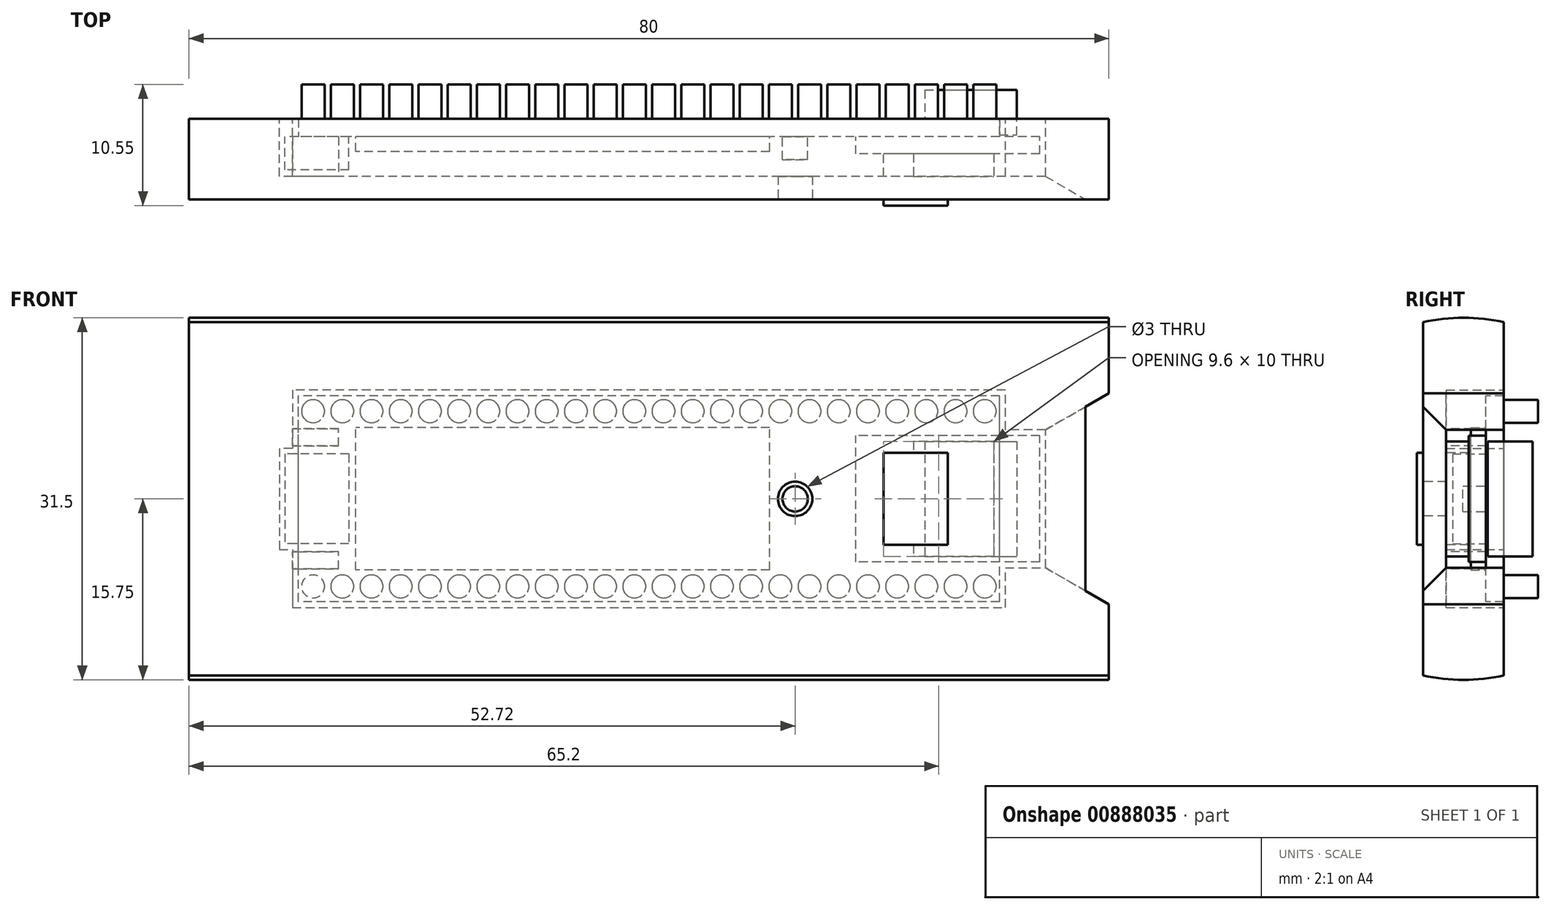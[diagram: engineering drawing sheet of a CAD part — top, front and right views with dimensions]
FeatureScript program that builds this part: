
annotation { "Feature Type Name" : "Feature", "Feature Type Description" : "" }
export const myFeature = defineFeature(function(context is Context, id is Id, definition is map)
    precondition{}
    {
        {
            var Q0;
            Q0=qCreatedBy(makeId("Front.planeOp"),FACE);
            var sketch = newSketch(context, id + "F0", { "sketchPlane" : qUnion([Q0])});
            skLineSegment(sketch, "E0.bottom", {"start": v(30.5, -8.95) * mm, "end": v(-30.5, -8.95) * mm});
            skLineSegment(sketch, "E0.top", {"start": v(30.5, 8.95) * mm, "end": v(-30.5, 8.95) * mm});
            skLineSegment(sketch, "E0.left", {"start": v(30.5, -8.95) * mm, "end": v(30.5, 8.95) * mm});
            skLineSegment(sketch, "E0.right", {"start": v(-30.5, -8.95) * mm, "end": v(-30.5, 8.95) * mm});
            skPoint(sketch, "E0.middle", {"position": v(0, 0) * mm});
            skCircle(sketch, "E1", {"center": v(12.72, 0) * mm, "radius": 1.1 * mm});
            skLineSegment(sketch, "E2.bottom", {"start": v(34, -5.5) * mm, "end": v(18, -5.5) * mm});
            skLineSegment(sketch, "E2.top", {"start": v(34, 5.5) * mm, "end": v(18, 5.5) * mm});
            skLineSegment(sketch, "E2.left", {"start": v(34, -5.5) * mm, "end": v(34, 5.5) * mm});
            skLineSegment(sketch, "E2.right", {"start": v(18, -5.5) * mm, "end": v(18, 5.5) * mm});
            skPoint(sketch, "E2.middle", {"position": v(26, 0) * mm});
            skLineSegment(sketch, "E3.bottom", {"start": v(-26.1, 3.9) * mm, "end": v(-31.65, 3.9) * mm});
            skLineSegment(sketch, "E3.top", {"start": v(-26.1, -3.9) * mm, "end": v(-31.65, -3.9) * mm});
            skLineSegment(sketch, "E3.left", {"start": v(-26.1, 3.9) * mm, "end": v(-26.1, -3.9) * mm});
            skLineSegment(sketch, "E3.right", {"start": v(-31.65, 3.9) * mm, "end": v(-31.65, -3.9) * mm});
            skPoint(sketch, "E3.middle", {"position": v(-28.87, 0) * mm});
            skLineSegment(sketch, "E4.bottom", {"start": v(10.5, -6.2) * mm, "end": v(-25.5, -6.2) * mm});
            skLineSegment(sketch, "E4.top", {"start": v(10.5, 6.2) * mm, "end": v(-25.5, 6.2) * mm});
            skLineSegment(sketch, "E4.left", {"start": v(10.5, -6.2) * mm, "end": v(10.5, 6.2) * mm});
            skLineSegment(sketch, "E4.right", {"start": v(-25.5, -6.2) * mm, "end": v(-25.5, 6.2) * mm});
            skPoint(sketch, "E4.middle", {"position": v(-7.5, 0) * mm});
            skSolve(sketch);
        }
        {
            var Q0;
            {var subQ8=sQuery(id+"F0.wireOp",EDGE,"E0.bottom");Q0=makeQuery(id+"F0.imprint","IMPRINT",FACE,{"disambiguationData":[TD([[makeQuery(id+"F0.imprint","IMPRINT",EDGE,{"derivedFrom":subQ8}),-1.0]])]});}
            var Q1;
            {var subQ5=sQuery(id+"F0.wireOp",EDGE,"E3.left");Q1=makeQuery(id+"F0.imprint","IMPRINT",FACE,{"disambiguationData":[TD([[makeQuery(id+"F0.imprint","IMPRINT",EDGE,{"derivedFrom":subQ5}),-1.0]])]});}
            var Q2;
            {var subQ5=sQuery(id+"F0.wireOp",EDGE,"E2.right");Q2=makeQuery(id+"F0.imprint","IMPRINT",FACE,{"disambiguationData":[TD([[makeQuery(id+"F0.imprint","IMPRINT",EDGE,{"derivedFrom":subQ5}),-1.0]])]});}
            var Q3;
            Q3=makeQuery(id+"F0.imprint","IMPRINT",FACE,{"disambiguationData":[TD([[makeQuery(id+"F0.imprint","IMPRINT",EDGE,{"derivedFrom":sQuery(id+"F0.wireOp",EDGE,"E1")}),1.0]])]});
            var Q4;
            Q4=makeQuery(id+"F0.imprint","IMPRINT",FACE,{"disambiguationData":[TD([[makeQuery(id+"F0.imprint","IMPRINT",EDGE,{"derivedFrom":sQuery(id+"F0.wireOp",EDGE,"E4.bottom")}),-1.0]])]});
            extrude(context, id + "F1", {"entities" : qUnion([Q0, Q1, Q2, Q3, Q4]), "oppositeDirection" : true, "depth" : 1.55 * mm, "offsetDistance" : 25 * mm});
        }
        {
            var Q0;
            Q0=makeQuery(id+"F0.imprint","IMPRINT",FACE,{"disambiguationData":[TD([[makeQuery(id+"F0.imprint","IMPRINT",EDGE,{"derivedFrom":sQuery(id+"F0.wireOp",EDGE,"E1")}),1.0]])]});
            extrude(context, id + "F2", {"entities" : qUnion([Q0]), "operationType" : NewBodyOperationType.ADD, "depth" : 2 * mm, "offsetDistance" : 25 * mm});
        }
        {
            var Q0;
            {var subQ5=sQuery(id+"F0.wireOp",EDGE,"E3.left");Q0=makeQuery(id+"F0.imprint","IMPRINT",FACE,{"disambiguationData":[TD([[makeQuery(id+"F0.imprint","IMPRINT",EDGE,{"derivedFrom":subQ5}),-1.0]])]});}
            var Q1;
            {var subQ5=sQuery(id+"F0.wireOp",EDGE,"E3.right");Q1=makeQuery(id+"F0.imprint","IMPRINT",FACE,{"disambiguationData":[TD([[makeQuery(id+"F0.imprint","IMPRINT",EDGE,{"derivedFrom":subQ5}),1.0]])]});}
            extrude(context, id + "F3", {"entities" : qUnion([Q0, Q1]), "operationType" : NewBodyOperationType.ADD, "depth" : 2.9 * mm, "offsetDistance" : 25 * mm});
        }
        {
            var Q0;
            {var subQ5=sQuery(id+"F0.wireOp",EDGE,"E2.left");Q0=makeQuery(id+"F0.imprint","IMPRINT",FACE,{"disambiguationData":[TD([[makeQuery(id+"F0.imprint","IMPRINT",EDGE,{"derivedFrom":subQ5}),1.0]])]});}
            var Q1;
            {var subQ5=sQuery(id+"F0.wireOp",EDGE,"E2.right");Q1=makeQuery(id+"F0.imprint","IMPRINT",FACE,{"disambiguationData":[TD([[makeQuery(id+"F0.imprint","IMPRINT",EDGE,{"derivedFrom":subQ5}),-1.0]])]});}
            extrude(context, id + "F4", {"entities" : qUnion([Q0, Q1]), "operationType" : NewBodyOperationType.ADD, "depth" : 1.5 * mm, "offsetDistance" : 25 * mm});
        }
        {
            var Q0;
            Q0=makeQuery(id+"F0.imprint","IMPRINT",FACE,{"disambiguationData":[TD([[makeQuery(id+"F0.imprint","IMPRINT",EDGE,{"derivedFrom":sQuery(id+"F0.wireOp",EDGE,"E4.bottom")}),-1.0]])]});
            extrude(context, id + "F5", {"entities" : qUnion([Q0]), "operationType" : NewBodyOperationType.ADD, "depth" : 1.3 * mm, "offsetDistance" : 25 * mm});
        }
        {
            var Q0;
            Q0=makeQuery(id+"F1.opExtrude","CAP_FACE",FACE,{"disambiguationData":[OSD([sQuery(id+"F0.wireOp",EDGE,"E0.bottom"),sQuery(id+"F0.wireOp",EDGE,"E0.top"),sQuery(id+"F0.wireOp",EDGE,"E0.left"),sQuery(id+"F0.wireOp",EDGE,"E0.right")])],"isStart":false});
            var sketch = newSketch(context, id + "F6", { "sketchPlane" : qUnion([Q0])});
            skCircle(sketch, "E5", {"center": v(29.21, -7.62) * mm, "radius": 1 * mm});
            skCircle(sketch, "E6.0.1.0", {"center": v(29.21, 7.62) * mm, "radius": 1 * mm});
            skCircle(sketch, "E6.1.0.0", {"center": v(26.67, -7.62) * mm, "radius": 1 * mm});
            skCircle(sketch, "E6.1.1.0", {"center": v(26.67, 7.62) * mm, "radius": 1 * mm});
            skCircle(sketch, "E6.2.0.0", {"center": v(24.13, -7.62) * mm, "radius": 1 * mm});
            skCircle(sketch, "E6.2.1.0", {"center": v(24.13, 7.62) * mm, "radius": 1 * mm});
            skCircle(sketch, "E6.3.0.0", {"center": v(21.6, -7.62) * mm, "radius": 1 * mm});
            skCircle(sketch, "E6.3.1.0", {"center": v(21.6, 7.62) * mm, "radius": 1 * mm});
            skCircle(sketch, "E6.4.0.0", {"center": v(19.05, -7.62) * mm, "radius": 1 * mm});
            skCircle(sketch, "E6.4.1.0", {"center": v(19.05, 7.62) * mm, "radius": 1 * mm});
            skCircle(sketch, "E6.5.0.0", {"center": v(16.51, -7.62) * mm, "radius": 1 * mm});
            skCircle(sketch, "E6.5.1.0", {"center": v(16.51, 7.62) * mm, "radius": 1 * mm});
            skCircle(sketch, "E6.6.0.0", {"center": v(13.97, -7.62) * mm, "radius": 1 * mm});
            skCircle(sketch, "E6.6.1.0", {"center": v(13.97, 7.62) * mm, "radius": 1 * mm});
            skCircle(sketch, "E6.7.0.0", {"center": v(11.43, -7.62) * mm, "radius": 1 * mm});
            skCircle(sketch, "E6.7.1.0", {"center": v(11.43, 7.62) * mm, "radius": 1 * mm});
            skCircle(sketch, "E6.8.0.0", {"center": v(8.9, -7.62) * mm, "radius": 1 * mm});
            skCircle(sketch, "E6.8.1.0", {"center": v(8.9, 7.62) * mm, "radius": 1 * mm});
            skCircle(sketch, "E6.9.0.0", {"center": v(6.35, -7.62) * mm, "radius": 1 * mm});
            skCircle(sketch, "E6.9.1.0", {"center": v(6.35, 7.62) * mm, "radius": 1 * mm});
            skCircle(sketch, "E6.10.0.0", {"center": v(3.81, -7.62) * mm, "radius": 1 * mm});
            skCircle(sketch, "E6.10.1.0", {"center": v(3.81, 7.62) * mm, "radius": 1 * mm});
            skCircle(sketch, "E6.11.0.0", {"center": v(1.27, -7.62) * mm, "radius": 1 * mm});
            skCircle(sketch, "E6.11.1.0", {"center": v(1.27, 7.62) * mm, "radius": 1 * mm});
            skCircle(sketch, "E6.12.0.0", {"center": v(-1.27, -7.62) * mm, "radius": 1 * mm});
            skCircle(sketch, "E6.12.1.0", {"center": v(-1.27, 7.62) * mm, "radius": 1 * mm});
            skCircle(sketch, "E6.13.0.0", {"center": v(-3.81, -7.62) * mm, "radius": 1 * mm});
            skCircle(sketch, "E6.13.1.0", {"center": v(-3.81, 7.62) * mm, "radius": 1 * mm});
            skCircle(sketch, "E6.14.0.0", {"center": v(-6.35, -7.62) * mm, "radius": 1 * mm});
            skCircle(sketch, "E6.14.1.0", {"center": v(-6.35, 7.62) * mm, "radius": 1 * mm});
            skCircle(sketch, "E6.15.0.0", {"center": v(-8.9, -7.62) * mm, "radius": 1 * mm});
            skCircle(sketch, "E6.15.1.0", {"center": v(-8.9, 7.62) * mm, "radius": 1 * mm});
            skCircle(sketch, "E6.16.0.0", {"center": v(-11.43, -7.62) * mm, "radius": 1 * mm});
            skCircle(sketch, "E6.16.1.0", {"center": v(-11.43, 7.62) * mm, "radius": 1 * mm});
            skCircle(sketch, "E6.17.0.0", {"center": v(-13.97, -7.62) * mm, "radius": 1 * mm});
            skCircle(sketch, "E6.17.1.0", {"center": v(-13.97, 7.62) * mm, "radius": 1 * mm});
            skCircle(sketch, "E6.18.0.0", {"center": v(-16.51, -7.62) * mm, "radius": 1 * mm});
            skCircle(sketch, "E6.18.1.0", {"center": v(-16.51, 7.62) * mm, "radius": 1 * mm});
            skCircle(sketch, "E6.19.0.0", {"center": v(-19.05, -7.62) * mm, "radius": 1 * mm});
            skCircle(sketch, "E6.19.1.0", {"center": v(-19.05, 7.62) * mm, "radius": 1 * mm});
            skCircle(sketch, "E6.20.0.0", {"center": v(-21.6, -7.62) * mm, "radius": 1 * mm});
            skCircle(sketch, "E6.20.1.0", {"center": v(-21.6, 7.62) * mm, "radius": 1 * mm});
            skCircle(sketch, "E6.21.0.0", {"center": v(-24.13, -7.62) * mm, "radius": 1 * mm});
            skCircle(sketch, "E6.21.1.0", {"center": v(-24.13, 7.62) * mm, "radius": 1 * mm});
            skCircle(sketch, "E6.22.0.0", {"center": v(-26.67, -7.62) * mm, "radius": 1 * mm});
            skCircle(sketch, "E6.22.1.0", {"center": v(-26.67, 7.62) * mm, "radius": 1 * mm});
            skCircle(sketch, "E6.23.0.0", {"center": v(-29.21, -7.62) * mm, "radius": 1 * mm});
            skCircle(sketch, "E6.23.1.0", {"center": v(-29.21, 7.62) * mm, "radius": 1 * mm});
            skLineSegment(sketch, "E6.direction1", {"start": v(29.21, -7.62) * mm, "end": v(26.67, -7.62) * mm, "construction": true});
            skLineSegment(sketch, "E6.direction2", {"start": v(29.21, -7.62) * mm, "end": v(29.21, 7.62) * mm, "construction": true});
            skSolve(sketch);
        }
        {
            var Q0;
            Q0=qSketchRegion(id+"F6",true);
            extrude(context, id + "F7", {"entities" : qUnion([Q0]), "operationType" : NewBodyOperationType.ADD, "depth" : 3 * mm, "offsetDistance" : 25 * mm});
        }
        {
            var Q0;
            Q0=makeQuery(id+"F4.opExtrude","CAP_FACE",FACE,{"disambiguationData":[OSD([sQuery(id+"F0.wireOp",EDGE,"E2.bottom"),sQuery(id+"F0.wireOp",EDGE,"E2.top"),sQuery(id+"F0.wireOp",EDGE,"E2.left"),sQuery(id+"F0.wireOp",EDGE,"E2.right")])],"isStart":false});
            var sketch = newSketch(context, id + "F8", { "sketchPlane" : qUnion([Q0])});
            skLineSegment(sketch, "E7.bottom", {"start": v(26, -4) * mm, "end": v(20.4, -4) * mm});
            skLineSegment(sketch, "E7.top", {"start": v(26, 4) * mm, "end": v(20.4, 4) * mm});
            skLineSegment(sketch, "E7.left", {"start": v(26, -4) * mm, "end": v(26, 4) * mm});
            skLineSegment(sketch, "E7.right", {"start": v(20.4, -4) * mm, "end": v(20.4, 4) * mm});
            skPoint(sketch, "E7.middle", {"position": v(23.2, 0) * mm});
            skSolve(sketch);
        }
        {
            var Q0;
            Q0=makeQuery(id+"F1.opExtrude","CAP_FACE",FACE,{"disambiguationData":[OSD([sQuery(id+"F0.wireOp",EDGE,"E0.bottom"),sQuery(id+"F0.wireOp",EDGE,"E0.top"),sQuery(id+"F0.wireOp",EDGE,"E0.left"),sQuery(id+"F0.wireOp",EDGE,"E0.right")])],"isStart":false});
            var sketch = newSketch(context, id + "F9", { "sketchPlane" : qUnion([Q0])});
            skLineSegment(sketch, "E8.bottom", {"start": v(-24, 5) * mm, "end": v(-32, 5) * mm});
            skLineSegment(sketch, "E8.top", {"start": v(-24, -5) * mm, "end": v(-32, -5) * mm});
            skLineSegment(sketch, "E8.left", {"start": v(-24, 5) * mm, "end": v(-24, -5) * mm});
            skLineSegment(sketch, "E8.right", {"start": v(-32, 5) * mm, "end": v(-32, -5) * mm});
            skPoint(sketch, "E8.middle", {"position": v(-28, 0) * mm});
            skLineSegment(sketch, "E9", {"start": v(-30.5, -5) * mm, "end": v(-30.5, 5) * mm});
            skSolve(sketch);
        }
        {
            var Q0;
            Q0=makeQuery(id+"F8.imprint","IMPRINT",FACE,{"disambiguationData":[TD([[makeQuery(id+"F8.imprint","IMPRINT",EDGE,{"derivedFrom":sQuery(id+"F8.wireOp",EDGE,"E7.bottom")}),-1.0]])]});
            extrude(context, id + "F10", {"entities" : qUnion([Q0]), "depth" : 4.5 * mm, "offsetDistance" : 25 * mm});
        }
        {
            var Q0;
            {var subQ0=sQuery(id+"F9.wireOp",EDGE,"E8.right");Q0=makeQuery(id+"F9.imprint","IMPRINT",FACE,{"disambiguationData":[TD([[makeQuery(id+"F9.imprint","IMPRINT",EDGE,{"derivedFrom":subQ0}),1.0]])]});}
            extrude(context, id + "F11", {"entities" : qUnion([Q0]), "oppositeDirection" : true, "depth" : 1.4 * mm, "offsetDistance" : 25 * mm});
        }
        {
            var Q0;
            {var subQ0=sQuery(id+"F9.wireOp",EDGE,"E8.right");Q0=makeQuery(id+"F9.imprint","IMPRINT",FACE,{"disambiguationData":[TD([[makeQuery(id+"F9.imprint","IMPRINT",EDGE,{"derivedFrom":subQ0}),1.0]])]});}
            var Q1;
            {var subQ0=sQuery(id+"F9.wireOp",EDGE,"E8.left");Q1=makeQuery(id+"F9.imprint","IMPRINT",FACE,{"disambiguationData":[TD([[makeQuery(id+"F9.imprint","IMPRINT",EDGE,{"derivedFrom":subQ0}),-1.0]])]});}
            extrude(context, id + "F12", {"entities" : qUnion([Q0, Q1]), "operationType" : NewBodyOperationType.ADD, "depth" : 2.5 * mm, "offsetDistance" : 25 * mm});
        }
        {
            var Q0;
            {var subQ1=sQuery(id+"F9.wireOp",EDGE,"E8.left");Q0=makeQuery(id+"F9.imprint","IMPRINT",FACE,{"disambiguationData":[TD([[makeQuery(id+"F9.imprint","IMPRINT",EDGE,{"derivedFrom":subQ1}),1.0]])]});}
            var sketch = newSketch(context, id + "F13", { "sketchPlane" : qUnion([Q0])});
            skLineSegment(sketch, "E10.bottom", {"start": v(-40, -17.5) * mm, "end": v(40, -17.5) * mm});
            skLineSegment(sketch, "E10.top", {"start": v(-40, 17.5) * mm, "end": v(40, 17.5) * mm});
            skLineSegment(sketch, "E10.left", {"start": v(-40, -17.5) * mm, "end": v(-40, 17.5) * mm});
            skLineSegment(sketch, "E10.right", {"start": v(40, -17.5) * mm, "end": v(40, 17.5) * mm});
            skPoint(sketch, "E10.middle", {"position": v(0, 0) * mm});
            skLineSegment(sketch, "E11", {"start": v(30.5, 8.95) * mm, "end": v(30.5, 3.9) * mm, "construction": true});
            skLineSegment(sketch, "E12", {"start": v(30.5, 3.9) * mm, "end": v(31.65, 3.9) * mm, "construction": true});
            skLineSegment(sketch, "E13", {"start": v(31.65, 3.9) * mm, "end": v(31.65, -3.9) * mm, "construction": true});
            skLineSegment(sketch, "E14", {"start": v(31.65, -3.9) * mm, "end": v(30.5, -3.9) * mm, "construction": true});
            skLineSegment(sketch, "E15", {"start": v(30.5, -3.9) * mm, "end": v(30.5, -8.95) * mm, "construction": true});
            skLineSegment(sketch, "E16", {"start": v(30.5, -8.95) * mm, "end": v(-30.5, -8.95) * mm, "construction": true});
            skLineSegment(sketch, "E17", {"start": v(-30.5, -8.95) * mm, "end": v(-30.5, -5.5) * mm, "construction": true});
            skLineSegment(sketch, "E18", {"start": v(-30.5, -5.5) * mm, "end": v(-34, -5.5) * mm, "construction": true});
            skLineSegment(sketch, "E19", {"start": v(-34, -5.5) * mm, "end": v(-34, 5.5) * mm, "construction": true});
            skLineSegment(sketch, "E20", {"start": v(-34, 5.5) * mm, "end": v(-30.5, 5.5) * mm, "construction": true});
            skLineSegment(sketch, "E21", {"start": v(-30.5, 5.5) * mm, "end": v(-30.5, 8.95) * mm, "construction": true});
            skLineSegment(sketch, "E22", {"start": v(-30.5, 8.95) * mm, "end": v(30.5, 8.95) * mm, "construction": true});
            skLineSegment(sketch, "E23.0", {"start": v(-31, 6) * mm, "end": v(-31, 9.45) * mm});
            skLineSegment(sketch, "E23.1", {"start": v(32.15, -4.4) * mm, "end": v(31, -4.4) * mm});
            skLineSegment(sketch, "E23.2", {"start": v(32.15, 4.4) * mm, "end": v(32.15, -4.4) * mm});
            skLineSegment(sketch, "E23.3", {"start": v(31, 4.4) * mm, "end": v(32.15, 4.4) * mm});
            skLineSegment(sketch, "E23.4", {"start": v(31, 9.45) * mm, "end": v(31, 4.4) * mm});
            skLineSegment(sketch, "E23.5", {"start": v(31, -4.4) * mm, "end": v(31, -9.45) * mm});
            skLineSegment(sketch, "E23.6", {"start": v(-31, 9.45) * mm, "end": v(31, 9.45) * mm});
            skLineSegment(sketch, "E23.7", {"start": v(31, -9.45) * mm, "end": v(-31, -9.45) * mm});
            skLineSegment(sketch, "E23.8", {"start": v(-31, -9.45) * mm, "end": v(-31, -6) * mm});
            skLineSegment(sketch, "E23.9", {"start": v(-31, -6) * mm, "end": v(-34.5, -6) * mm});
            skLineSegment(sketch, "E23.10", {"start": v(-34.5, -6) * mm, "end": v(-34.5, 6) * mm});
            skLineSegment(sketch, "E23.11", {"start": v(-34.5, 6) * mm, "end": v(-31, 6) * mm});
            skLineSegment(sketch, "E24", {"start": v(31, 4.4) * mm, "end": v(31, -4.4) * mm});
            skLineSegment(sketch, "E25", {"start": v(-31, 6) * mm, "end": v(-31, -6) * mm});
            skLineSegment(sketch, "E26.bottom", {"start": v(27, 2.25) * mm, "end": v(29.5, 2.25) * mm});
            skLineSegment(sketch, "E26.top", {"start": v(27, -2.25) * mm, "end": v(29.5, -2.25) * mm});
            skLineSegment(sketch, "E26.left", {"start": v(27, 2.25) * mm, "end": v(27, -2.25) * mm});
            skLineSegment(sketch, "E26.right", {"start": v(29.5, 2.25) * mm, "end": v(29.5, -2.25) * mm});
            skPoint(sketch, "E26.middle", {"position": v(28.25, 0) * mm});
            skLineSegment(sketch, "E27.bottom", {"start": v(-25.25, -3.75) * mm, "end": v(-20.75, -3.75) * mm});
            skLineSegment(sketch, "E27.top", {"start": v(-25.25, 3.75) * mm, "end": v(-20.75, 3.75) * mm});
            skLineSegment(sketch, "E27.left", {"start": v(-25.25, -3.75) * mm, "end": v(-25.25, 3.75) * mm});
            skLineSegment(sketch, "E27.right", {"start": v(-20.75, -3.75) * mm, "end": v(-20.75, 3.75) * mm});
            skPoint(sketch, "E27.middle", {"position": v(-23, 0) * mm});
            skSolve(sketch);
        }
        {
            var Q0;
            Q0=makeQuery(id+"F13.imprint","IMPRINT",FACE,{"disambiguationData":[TD([[makeQuery(id+"F13.imprint","IMPRINT",EDGE,{"derivedFrom":sQuery(id+"F13.wireOp",EDGE,"E10.bottom")}),1.0]])]});
            extrude(context, id + "F14", {"entities" : qUnion([Q0]), "oppositeDirection" : true, "depth" : 7 * mm, "offsetDistance" : 25 * mm});
        }
        {
            var Q0;
            Q0=makeQuery(id+"F14.opExtrude","CAP_FACE",FACE,{"disambiguationData":[OSD([sQuery(id+"F13.wireOp",EDGE,"E10.bottom"),sQuery(id+"F13.wireOp",EDGE,"E10.top"),sQuery(id+"F13.wireOp",EDGE,"E10.left"),sQuery(id+"F13.wireOp",EDGE,"E10.right"),sQuery(id+"F13.wireOp",EDGE,"E23.0"),sQuery(id+"F13.wireOp",EDGE,"E23.1"),sQuery(id+"F13.wireOp",EDGE,"E23.2"),sQuery(id+"F13.wireOp",EDGE,"E23.3"),sQuery(id+"F13.wireOp",EDGE,"E23.4"),sQuery(id+"F13.wireOp",EDGE,"E23.5"),sQuery(id+"F13.wireOp",EDGE,"E23.6"),sQuery(id+"F13.wireOp",EDGE,"E23.7"),sQuery(id+"F13.wireOp",EDGE,"E23.8"),sQuery(id+"F13.wireOp",EDGE,"E23.9"),sQuery(id+"F13.wireOp",EDGE,"E23.10"),sQuery(id+"F13.wireOp",EDGE,"E23.11")])],"isStart":false});
            var sketch = newSketch(context, id + "F15", { "sketchPlane" : qUnion([Q0])});
            skLineSegment(sketch, "E28.bottom", {"start": v(-31, 6.1) * mm, "end": v(-27, 6.1) * mm});
            skLineSegment(sketch, "E28.top", {"start": v(-31, 4.6) * mm, "end": v(-27, 4.6) * mm});
            skLineSegment(sketch, "E28.left", {"start": v(-31, 6.1) * mm, "end": v(-31, 4.6) * mm});
            skLineSegment(sketch, "E28.right", {"start": v(-27, 6.1) * mm, "end": v(-27, 4.6) * mm});
            skLineSegment(sketch, "E29.bottom", {"start": v(-27, -4.6) * mm, "end": v(-31, -4.6) * mm});
            skLineSegment(sketch, "E29.top", {"start": v(-27, -6.1) * mm, "end": v(-31, -6.1) * mm});
            skLineSegment(sketch, "E29.left", {"start": v(-27, -4.6) * mm, "end": v(-27, -6.1) * mm});
            skLineSegment(sketch, "E29.right", {"start": v(-31, -4.6) * mm, "end": v(-31, -6.1) * mm});
            skLineSegment(sketch, "E30.bottom", {"start": v(23, -5) * mm, "end": v(30, -5) * mm});
            skLineSegment(sketch, "E30.top", {"start": v(23, 5) * mm, "end": v(30, 5) * mm});
            skLineSegment(sketch, "E30.left", {"start": v(23, -5) * mm, "end": v(23, 5) * mm});
            skLineSegment(sketch, "E30.right", {"start": v(30, -5) * mm, "end": v(30, 5) * mm});
            skPoint(sketch, "E30.middle", {"position": v(26.5, 0) * mm});
            skSolve(sketch);
        }
        {
            var Q0;
            Q0=makeQuery(id+"F15.imprint","IMPRINT",FACE,{"disambiguationData":[TD([[makeQuery(id+"F15.imprint","IMPRINT",EDGE,{"derivedFrom":makeQuery(id+"F14.opExtrude","CAP_EDGE",EDGE,{"disambiguationData":[OSD([sQuery(id+"F13.wireOp",EDGE,"E23.0")])],"isStart":false})}),1.0]])]});
            extrude(context, id + "F16", {"entities" : qUnion([Q0]), "operationType" : NewBodyOperationType.ADD, "oppositeDirection" : true, "depth" : 2 * mm, "offsetDistance" : 25 * mm});
        }
        {
            var Q0;
            Q0=makeQuery(id+"F15.imprint","IMPRINT",FACE,{"disambiguationData":[TD([[makeQuery(id+"F15.imprint","IMPRINT",EDGE,{"derivedFrom":sQuery(id+"F15.wireOp",EDGE,"E28.bottom")}),-1.0]])]});
            var Q1;
            Q1=makeQuery(id+"F15.imprint","IMPRINT",FACE,{"disambiguationData":[TD([[makeQuery(id+"F15.imprint","IMPRINT",EDGE,{"derivedFrom":sQuery(id+"F15.wireOp",EDGE,"E29.bottom")}),1.0]])]});
            var Q2;
            Q2=makeQuery(id+"F1.opExtrude","CAP_FACE",FACE,{"disambiguationData":[OSD([sQuery(id+"F0.wireOp",EDGE,"E0.bottom"),sQuery(id+"F0.wireOp",EDGE,"E0.top"),sQuery(id+"F0.wireOp",EDGE,"E0.left"),sQuery(id+"F0.wireOp",EDGE,"E0.right")])],"isStart":true});
            extrude(context, id + "F17", {"entities" : qUnion([Q0, Q1]), "operationType" : NewBodyOperationType.ADD, "endBound" : BoundingType.UP_TO_SURFACE, "oppositeDirection" : true, "depth" : 5 * mm, "endBoundEntityFace" : qUnion([Q2]), "offsetDistance" : 25 * mm});
        }
        {
            var Q0;
            Q0=makeQuery(id+"F15.imprint","IMPRINT",FACE,{"disambiguationData":[TD([[makeQuery(id+"F15.imprint","IMPRINT",EDGE,{"derivedFrom":sQuery(id+"F15.wireOp",EDGE,"E30.bottom")}),1.0]])]});
            var Q1;
            Q1=makeQuery(id+"F4.opExtrude","CAP_FACE",FACE,{"disambiguationData":[OSD([sQuery(id+"F0.wireOp",EDGE,"E2.bottom"),sQuery(id+"F0.wireOp",EDGE,"E2.top"),sQuery(id+"F0.wireOp",EDGE,"E2.left"),sQuery(id+"F0.wireOp",EDGE,"E2.right")])],"isStart":false});
            extrude(context, id + "F18", {"entities" : qUnion([Q0]), "operationType" : NewBodyOperationType.ADD, "endBound" : BoundingType.UP_TO_SURFACE, "oppositeDirection" : true, "depth" : 25 * mm, "endBoundEntityFace" : qUnion([Q1]), "offsetDistance" : 25 * mm});
        }
        {
            var Q0;
            {var subQ3=sQuery(id+"F15.wireOp",EDGE,"E28.left");Q0=makeQuery(id+"F15.imprint","IMPRINT",FACE,{"disambiguationData":[TD([[makeQuery(id+"F15.imprint","IMPRINT",EDGE,{"derivedFrom":subQ3}),-1.0]])]});}
            var sketch = newSketch(context, id + "F19", { "sketchPlane" : qUnion([Q0])});
            skCircle(sketch, "E31", {"center": v(12.72, 0) * mm, "radius": 1.5 * mm});
            skSolve(sketch);
        }
        {
            var Q0;
            Q0=makeQuery(id+"F19.imprint","IMPRINT",FACE,{"disambiguationData":[TD([[makeQuery(id+"F19.imprint","IMPRINT",EDGE,{"derivedFrom":sQuery(id+"F19.wireOp",EDGE,"E31")}),1.0]])]});
            extrude(context, id + "F20", {"entities" : qUnion([Q0]), "operationType" : NewBodyOperationType.REMOVE, "endBound" : BoundingType.UP_TO_NEXT, "oppositeDirection" : true, "depth" : 25 * mm, "offsetDistance" : 25 * mm});
        }
        {
            var Q0;
            Q0=makeQuery(id+"F14.opExtrude","SWEPT_FACE",FACE,{"disambiguationData":[OSD([sQuery(id+"F13.wireOp",EDGE,"E23.10")])]});
            var sketch = newSketch(context, id + "F21", { "sketchPlane" : qUnion([Q0])});
            skLineSegment(sketch, "E32.bottom", {"start": v(1.5, -5.5) * mm, "end": v(0, -5.5) * mm, "construction": true});
            skLineSegment(sketch, "E32.top", {"start": v(1.5, 5.5) * mm, "end": v(0, 5.5) * mm, "construction": true});
            skLineSegment(sketch, "E32.left", {"start": v(1.5, -5.5) * mm, "end": v(1.5, 5.5) * mm, "construction": true});
            skLineSegment(sketch, "E32.right", {"start": v(0, -5.5) * mm, "end": v(0, 5.5) * mm, "construction": true});
            skLineSegment(sketch, "E33.0", {"start": v(4.5, -8.5) * mm, "end": v(4.5, 8.5) * mm});
            skLineSegment(sketch, "E33.1", {"start": v(4.5, -8.5) * mm, "end": v(-3, -8.5) * mm});
            skLineSegment(sketch, "E33.2", {"start": v(-3, -8.5) * mm, "end": v(-3, 8.5) * mm});
            skLineSegment(sketch, "E33.3", {"start": v(4.5, 8.5) * mm, "end": v(-3, 8.5) * mm});
            skSolve(sketch);
        }
        {
            var Q0;
            {var subQ0=sQuery(id+"F13.wireOp",EDGE,"E23.10");Q0=makeQuery(id+"F21.imprint","IMPRINT",FACE,{"disambiguationData":[TD([[makeQuery(id+"F21.imprint","IMPRINT",EDGE,{"derivedFrom":makeQuery(id+"F14.opExtrude","CAP_EDGE",EDGE,{"disambiguationData":[OSD([subQ0])],"isStart":true})}),-1.0]])]});}
            var Q1;
            Q1=makeQuery(id+"F14.opExtrude","SWEPT_FACE",FACE,{"disambiguationData":[OSD([sQuery(id+"F13.wireOp",EDGE,"E10.left")])]});
            extrude(context, id + "F22", {"entities" : qUnion([Q0]), "operationType" : NewBodyOperationType.REMOVE, "endBound" : BoundingType.UP_TO_SURFACE, "oppositeDirection" : true, "depth" : 25 * mm, "endBoundEntityFace" : qUnion([Q1]), "offsetDistance" : 25 * mm, "hasDraft" : true, "draftAngle" : 30 * degree});
        }
        {
            var Q0;
            Q0=makeQuery(id+"F14.opExtrude","SWEPT_FACE",FACE,{"disambiguationData":[OSD([sQuery(id+"F13.wireOp",EDGE,"E10.right")])]});
            var sketch = newSketch(context, id + "F23", { "sketchPlane" : qUnion([Q0])});
            skArc(sketch, "E34", {"start": v(-1.55, -15.36) * mm, "mid": v(1.95, -15.75) * mm, "end": v(5.45, -15.36) * mm});
            skLineSegment(sketch, "E35.bottom", {"start": v(-1.55, 17.5) * mm, "end": v(5.45, 17.5) * mm});
            skLineSegment(sketch, "E35.top", {"start": v(-1.55, -17.5) * mm, "end": v(5.45, -17.5) * mm});
            skLineSegment(sketch, "E35.left", {"start": v(-1.55, 17.5) * mm, "end": v(-1.55, 15.36) * mm});
            skLineSegment(sketch, "E35.right", {"start": v(5.45, 17.5) * mm, "end": v(5.45, 15.36) * mm});
            skArc(sketch, "E36.trimOffspring", {"start": v(5.45, 15.36) * mm, "mid": v(1.95, 15.75) * mm, "end": v(-1.55, 15.36) * mm});
            skLineSegment(sketch, "E37.trimOffspring", {"start": v(5.45, -15.36) * mm, "end": v(5.45, -17.5) * mm});
            skLineSegment(sketch, "E38.trimOffspring", {"start": v(-1.55, -15.36) * mm, "end": v(-1.55, -17.5) * mm});
            skPoint(sketch, "E39.orphan", {"position": v(5.45, 0) * mm});
            skPoint(sketch, "E40.start.orphan", {"position": v(-1.55, 0) * mm});
            skSolve(sketch);
        }
        {
            var Q0;
            Q0=qSketchRegion(id+"F23",true);
            extrude(context, id + "F24", {"entities" : qUnion([Q0]), "operationType" : NewBodyOperationType.REMOVE, "oppositeDirection" : true, "depth" : 80 * mm, "offsetDistance" : 25 * mm});
        }
    });
